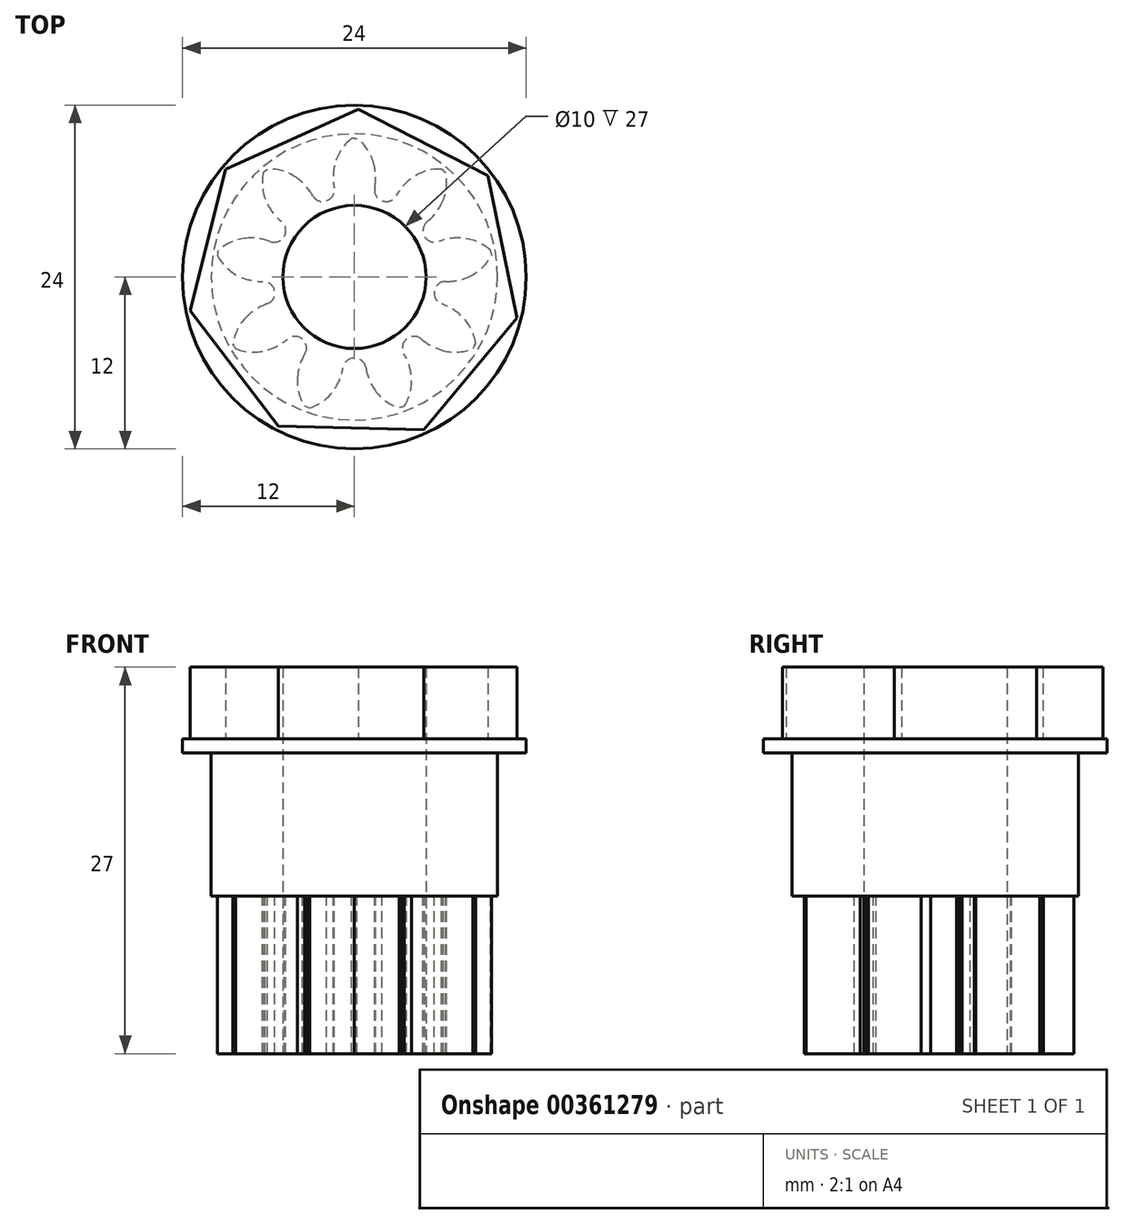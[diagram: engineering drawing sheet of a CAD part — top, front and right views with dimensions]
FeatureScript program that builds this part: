
annotation { "Feature Type Name" : "Feature", "Feature Type Description" : "" }
export const myFeature = defineFeature(function(context is Context, id is Id, definition is map)
    precondition{}
    {
        {
            var Q0;
            Q0=qCreatedBy(makeId("Top.planeOp"),FACE);
            var sketch = newSketch(context, id + "F0", { "sketchPlane" : qUnion([Q0])});
            skCircle(sketch, "E0", {"center": v(0, 0) * mm, "radius": 7.9 * mm, "construction": true});
            skCircle(sketch, "E1", {"center": v(0, 0) * mm, "radius": 9.68 * mm, "construction": true});
            skCircle(sketch, "E2", {"center": v(0, 0) * mm, "radius": 5.68 * mm, "construction": true});
            skCircle(sketch, "E3", {"center": v(0, 7.9) * mm, "radius": 1.4 * mm, "construction": true});
            skCircle(sketch, "E4", {"center": v(0, 0) * mm, "radius": 7.3 * mm, "construction": true});
            skCircle(sketch, "E5", {"center": v(1.39, 7.78) * mm, "radius": 3.3 * mm, "construction": true});
            skCircle(sketch, "E6", {"center": v(0, 0) * mm, "radius": 5 * mm});
            skCircle(sketch, "E7", {"center": v(1.39, 7.78) * mm, "radius": 3.77 * mm, "construction": true});
            skArc(sketch, "E8", {"start": v(1.42, 6.23) * mm, "mid": v(1.48, 7) * mm, "end": v(1.39, 7.78) * mm});
            skArc(sketch, "E9.trimOffspring", {"start": v(1.39, 7.78) * mm, "mid": v(0.96, 8.83) * mm, "end": v(0.19, 9.68) * mm});
            skLineSegment(sketch, "E10", {"start": v(2.17, 5.25) * mm, "end": v(1.96, 5.31) * mm});
            skLineSegment(sketch, "E11", {"start": v(0, 9.68) * mm, "end": v(0.19, 9.68) * mm});
            skPoint(sketch, "E12.visualSharp", {"position": v(1.22, 5.55) * mm});
            skArc(sketch, "E12.filletArc", {"start": v(1.42, 6.23) * mm, "mid": v(1.52, 5.67) * mm, "end": v(1.96, 5.31) * mm});
            skLineSegment(sketch, "E13.MirrorCS", {"start": v(-2.17, 5.25) * mm, "end": v(-1.96, 5.31) * mm});
            skLineSegment(sketch, "E14.MirrorCS", {"start": v(0, 9.68) * mm, "end": v(-0.19, 9.68) * mm});
            skArc(sketch, "E15.MirrorCS", {"start": v(-1.39, 7.78) * mm, "mid": v(-0.96, 8.83) * mm, "end": v(-0.19, 9.68) * mm});
            skArc(sketch, "E16.MirrorCS", {"start": v(-1.42, 6.23) * mm, "mid": v(-1.48, 7) * mm, "end": v(-1.39, 7.78) * mm});
            skArc(sketch, "E17.MirrorCS", {"start": v(-1.42, 6.23) * mm, "mid": v(-1.52, 5.67) * mm, "end": v(-1.96, 5.31) * mm});
            skLineSegment(sketch, "E18.1.0", {"start": v(-5.04, 2.62) * mm, "end": v(-4.92, 2.8) * mm});
            skArc(sketch, "E18.1.1", {"start": v(-5.09, 3.86) * mm, "mid": v(-4.8, 3.37) * mm, "end": v(-4.92, 2.8) * mm});
            skArc(sketch, "E18.1.2", {"start": v(-5.09, 3.86) * mm, "mid": v(-5.64, 4.41) * mm, "end": v(-6.06, 5.06) * mm});
            skArc(sketch, "E18.1.3", {"start": v(-6.06, 5.06) * mm, "mid": v(-6.4, 6.15) * mm, "end": v(-6.37, 7.3) * mm});
            skLineSegment(sketch, "E18.1.4", {"start": v(-6.22, 7.42) * mm, "end": v(-6.37, 7.3) * mm});
            skLineSegment(sketch, "E18.1.5", {"start": v(-6.22, 7.42) * mm, "end": v(-6.08, 7.54) * mm});
            skArc(sketch, "E18.1.6", {"start": v(-3.93, 6.85) * mm, "mid": v(-4.95, 7.38) * mm, "end": v(-6.08, 7.54) * mm});
            skArc(sketch, "E18.1.7", {"start": v(-2.92, 5.68) * mm, "mid": v(-3.37, 6.32) * mm, "end": v(-3.93, 6.85) * mm});
            skArc(sketch, "E18.1.8", {"start": v(-2.92, 5.68) * mm, "mid": v(-2.48, 5.32) * mm, "end": v(-1.91, 5.33) * mm});
            skLineSegment(sketch, "E18.1.9", {"start": v(-1.7, 5.42) * mm, "end": v(-1.91, 5.33) * mm});
            skLineSegment(sketch, "E18.2.0", {"start": v(-5.55, -1.23) * mm, "end": v(-5.57, -1.01) * mm});
            skArc(sketch, "E18.2.1", {"start": v(-6.38, -0.31) * mm, "mid": v(-5.84, -0.5) * mm, "end": v(-5.57, -1.01) * mm});
            skArc(sketch, "E18.2.2", {"start": v(-6.38, -0.31) * mm, "mid": v(-7.15, -0.25) * mm, "end": v(-7.9, -0.02) * mm});
            skArc(sketch, "E18.2.3", {"start": v(-7.9, -0.02) * mm, "mid": v(-8.86, 0.6) * mm, "end": v(-9.56, 1.5) * mm});
            skLineSegment(sketch, "E18.2.4", {"start": v(-9.53, 1.68) * mm, "end": v(-9.56, 1.5) * mm});
            skLineSegment(sketch, "E18.2.5", {"start": v(-9.53, 1.68) * mm, "end": v(-9.5, 1.87) * mm});
            skArc(sketch, "E18.2.6", {"start": v(-7.42, 2.72) * mm, "mid": v(-8.53, 2.48) * mm, "end": v(-9.5, 1.87) * mm});
            skArc(sketch, "E18.2.7", {"start": v(-5.89, 2.48) * mm, "mid": v(-6.64, 2.68) * mm, "end": v(-7.42, 2.72) * mm});
            skArc(sketch, "E18.2.8", {"start": v(-5.89, 2.48) * mm, "mid": v(-5.32, 2.48) * mm, "end": v(-4.9, 2.86) * mm});
            skLineSegment(sketch, "E18.2.9", {"start": v(-4.8, 3.05) * mm, "end": v(-4.9, 2.86) * mm});
            skLineSegment(sketch, "E18.3.0", {"start": v(-3.46, -4.5) * mm, "end": v(-3.62, -4.36) * mm});
            skArc(sketch, "E18.3.1", {"start": v(-4.68, -4.34) * mm, "mid": v(-4.15, -4.15) * mm, "end": v(-3.62, -4.36) * mm});
            skArc(sketch, "E18.3.2", {"start": v(-4.68, -4.34) * mm, "mid": v(-5.32, -4.79) * mm, "end": v(-6.04, -5.1) * mm});
            skArc(sketch, "E18.3.3", {"start": v(-6.04, -5.1) * mm, "mid": v(-7.17, -5.24) * mm, "end": v(-8.29, -5) * mm});
            skLineSegment(sketch, "E18.3.4", {"start": v(-8.38, -4.84) * mm, "end": v(-8.29, -5) * mm});
            skLineSegment(sketch, "E18.3.5", {"start": v(-8.38, -4.84) * mm, "end": v(-8.48, -4.68) * mm});
            skArc(sketch, "E18.3.6", {"start": v(-7.43, -2.69) * mm, "mid": v(-8.13, -3.59) * mm, "end": v(-8.48, -4.68) * mm});
            skArc(sketch, "E18.3.7", {"start": v(-6.1, -1.89) * mm, "mid": v(-6.8, -2.22) * mm, "end": v(-7.43, -2.69) * mm});
            skArc(sketch, "E18.3.8", {"start": v(-6.1, -1.89) * mm, "mid": v(-5.67, -1.52) * mm, "end": v(-5.58, -0.96) * mm});
            skLineSegment(sketch, "E18.3.9", {"start": v(-5.63, -0.74) * mm, "end": v(-5.58, -0.96) * mm});
            skLineSegment(sketch, "E18.4.0", {"start": v(0.25, -5.67) * mm, "end": v(0.03, -5.66) * mm});
            skArc(sketch, "E18.4.1", {"start": v(-0.8, -6.34) * mm, "mid": v(-0.51, -5.84) * mm, "end": v(0.03, -5.66) * mm});
            skArc(sketch, "E18.4.2", {"start": v(-0.8, -6.34) * mm, "mid": v(-1, -7.09) * mm, "end": v(-1.35, -7.78) * mm});
            skArc(sketch, "E18.4.3", {"start": v(-1.35, -7.78) * mm, "mid": v(-2.12, -8.63) * mm, "end": v(-3.13, -9.16) * mm});
            skLineSegment(sketch, "E18.4.4", {"start": v(-3.31, -9.1) * mm, "end": v(-3.13, -9.16) * mm});
            skLineSegment(sketch, "E18.4.5", {"start": v(-3.31, -9.1) * mm, "end": v(-3.49, -9.03) * mm});
            skArc(sketch, "E18.4.6", {"start": v(-3.97, -6.83) * mm, "mid": v(-3.92, -7.97) * mm, "end": v(-3.49, -9.03) * mm});
            skArc(sketch, "E18.4.7", {"start": v(-3.46, -5.37) * mm, "mid": v(-3.79, -6.07) * mm, "end": v(-3.97, -6.83) * mm});
            skArc(sketch, "E18.4.8", {"start": v(-3.46, -5.37) * mm, "mid": v(-3.36, -4.8) * mm, "end": v(-3.66, -4.32) * mm});
            skLineSegment(sketch, "E18.4.9", {"start": v(-3.84, -4.19) * mm, "end": v(-3.66, -4.32) * mm});
            skLineSegment(sketch, "E18.5.0", {"start": v(3.84, -4.19) * mm, "end": v(3.66, -4.32) * mm});
            skArc(sketch, "E18.5.1", {"start": v(3.46, -5.37) * mm, "mid": v(3.36, -4.8) * mm, "end": v(3.66, -4.32) * mm});
            skArc(sketch, "E18.5.2", {"start": v(3.46, -5.37) * mm, "mid": v(3.79, -6.07) * mm, "end": v(3.97, -6.83) * mm});
            skArc(sketch, "E18.5.3", {"start": v(3.97, -6.83) * mm, "mid": v(3.92, -7.97) * mm, "end": v(3.49, -9.03) * mm});
            skLineSegment(sketch, "E18.5.4", {"start": v(3.31, -9.1) * mm, "end": v(3.49, -9.03) * mm});
            skLineSegment(sketch, "E18.5.5", {"start": v(3.31, -9.1) * mm, "end": v(3.13, -9.16) * mm});
            skArc(sketch, "E18.5.6", {"start": v(1.35, -7.78) * mm, "mid": v(2.12, -8.63) * mm, "end": v(3.13, -9.16) * mm});
            skArc(sketch, "E18.5.7", {"start": v(0.8, -6.34) * mm, "mid": v(1, -7.09) * mm, "end": v(1.35, -7.78) * mm});
            skArc(sketch, "E18.5.8", {"start": v(0.8, -6.34) * mm, "mid": v(0.51, -5.84) * mm, "end": v(-0.03, -5.66) * mm});
            skLineSegment(sketch, "E18.5.9", {"start": v(-0.25, -5.67) * mm, "end": v(-0.03, -5.66) * mm});
            skLineSegment(sketch, "E18.6.0", {"start": v(5.63, -0.74) * mm, "end": v(5.58, -0.96) * mm});
            skArc(sketch, "E18.6.1", {"start": v(6.1, -1.89) * mm, "mid": v(5.67, -1.52) * mm, "end": v(5.58, -0.96) * mm});
            skArc(sketch, "E18.6.2", {"start": v(6.1, -1.89) * mm, "mid": v(6.8, -2.22) * mm, "end": v(7.43, -2.69) * mm});
            skArc(sketch, "E18.6.3", {"start": v(7.43, -2.69) * mm, "mid": v(8.13, -3.59) * mm, "end": v(8.48, -4.68) * mm});
            skLineSegment(sketch, "E18.6.4", {"start": v(8.38, -4.84) * mm, "end": v(8.48, -4.68) * mm});
            skLineSegment(sketch, "E18.6.5", {"start": v(8.38, -4.84) * mm, "end": v(8.29, -5) * mm});
            skArc(sketch, "E18.6.6", {"start": v(6.04, -5.1) * mm, "mid": v(7.17, -5.24) * mm, "end": v(8.29, -5) * mm});
            skArc(sketch, "E18.6.7", {"start": v(4.68, -4.34) * mm, "mid": v(5.32, -4.79) * mm, "end": v(6.04, -5.1) * mm});
            skArc(sketch, "E18.6.8", {"start": v(4.68, -4.34) * mm, "mid": v(4.15, -4.15) * mm, "end": v(3.62, -4.36) * mm});
            skLineSegment(sketch, "E18.6.9", {"start": v(3.46, -4.5) * mm, "end": v(3.62, -4.36) * mm});
            skLineSegment(sketch, "E18.7.0", {"start": v(4.8, 3.05) * mm, "end": v(4.9, 2.86) * mm});
            skArc(sketch, "E18.7.1", {"start": v(5.89, 2.48) * mm, "mid": v(5.32, 2.48) * mm, "end": v(4.9, 2.86) * mm});
            skArc(sketch, "E18.7.2", {"start": v(5.89, 2.48) * mm, "mid": v(6.64, 2.68) * mm, "end": v(7.42, 2.72) * mm});
            skArc(sketch, "E18.7.3", {"start": v(7.42, 2.72) * mm, "mid": v(8.53, 2.48) * mm, "end": v(9.5, 1.87) * mm});
            skLineSegment(sketch, "E18.7.4", {"start": v(9.53, 1.68) * mm, "end": v(9.5, 1.87) * mm});
            skLineSegment(sketch, "E18.7.5", {"start": v(9.53, 1.68) * mm, "end": v(9.56, 1.5) * mm});
            skArc(sketch, "E18.7.6", {"start": v(7.9, -0.02) * mm, "mid": v(8.86, 0.6) * mm, "end": v(9.56, 1.5) * mm});
            skArc(sketch, "E18.7.7", {"start": v(6.38, -0.31) * mm, "mid": v(7.15, -0.25) * mm, "end": v(7.9, -0.02) * mm});
            skArc(sketch, "E18.7.8", {"start": v(6.38, -0.31) * mm, "mid": v(5.84, -0.5) * mm, "end": v(5.57, -1.01) * mm});
            skLineSegment(sketch, "E18.7.9", {"start": v(5.55, -1.23) * mm, "end": v(5.57, -1.01) * mm});
            skLineSegment(sketch, "E18.8.0", {"start": v(1.7, 5.42) * mm, "end": v(1.91, 5.33) * mm});
            skArc(sketch, "E18.8.1", {"start": v(2.92, 5.68) * mm, "mid": v(2.48, 5.32) * mm, "end": v(1.91, 5.33) * mm});
            skArc(sketch, "E18.8.2", {"start": v(2.92, 5.68) * mm, "mid": v(3.37, 6.32) * mm, "end": v(3.93, 6.85) * mm});
            skArc(sketch, "E18.8.3", {"start": v(3.93, 6.85) * mm, "mid": v(4.95, 7.38) * mm, "end": v(6.08, 7.54) * mm});
            skLineSegment(sketch, "E18.8.4", {"start": v(6.22, 7.42) * mm, "end": v(6.08, 7.54) * mm});
            skLineSegment(sketch, "E18.8.5", {"start": v(6.22, 7.42) * mm, "end": v(6.37, 7.3) * mm});
            skArc(sketch, "E18.8.6", {"start": v(6.06, 5.06) * mm, "mid": v(6.4, 6.15) * mm, "end": v(6.37, 7.3) * mm});
            skArc(sketch, "E18.8.7", {"start": v(5.09, 3.86) * mm, "mid": v(5.64, 4.41) * mm, "end": v(6.06, 5.06) * mm});
            skArc(sketch, "E18.8.8", {"start": v(5.09, 3.86) * mm, "mid": v(4.8, 3.37) * mm, "end": v(4.92, 2.8) * mm});
            skLineSegment(sketch, "E18.8.9", {"start": v(5.04, 2.62) * mm, "end": v(4.92, 2.8) * mm});
            skCircle(sketch, "E19", {"center": v(0, 0) * mm, "radius": 10 * mm});
            skCircle(sketch, "E20.cCircle", {"center": v(0, 0) * mm, "radius": 10.55 * mm, "construction": true});
            skLineSegment(sketch, "E20.0", {"start": v(11.35, -2.87) * mm, "end": v(4.84, -10.66) * mm});
            skLineSegment(sketch, "E20.1", {"start": v(4.84, -10.66) * mm, "end": v(-5.32, -10.43) * mm});
            skLineSegment(sketch, "E20.2", {"start": v(-5.32, -10.43) * mm, "end": v(-11.47, -2.34) * mm});
            skLineSegment(sketch, "E20.3", {"start": v(-11.47, -2.34) * mm, "end": v(-8.98, 7.5) * mm});
            skLineSegment(sketch, "E20.4", {"start": v(-8.98, 7.5) * mm, "end": v(0.27, 11.7) * mm});
            skLineSegment(sketch, "E20.5", {"start": v(0.27, 11.7) * mm, "end": v(9.32, 7.09) * mm});
            skLineSegment(sketch, "E20.6", {"start": v(9.32, 7.09) * mm, "end": v(11.35, -2.87) * mm});
            skPoint(sketch, "E20.0.midPoint", {"position": v(8.1, -6.77) * mm});
            skCircle(sketch, "E21", {"center": v(0, 0) * mm, "radius": 12 * mm});
            skSolve(sketch);
        }
        {
            var Q0;
            Q0=makeQuery(id+"F0.imprint","IMPRINT",FACE,{"disambiguationData":[TD([[makeQuery(id+"F0.imprint","IMPRINT",EDGE,{"derivedFrom":sQuery(id+"F0.wireOp",EDGE,"E6")}),-1.0]])]});
            extrude(context, id + "F1", {"entities" : qUnion([Q0]), "depth" : 16 * mm});
        }
        {
            var Q0;
            {var subQ80=sQuery(id+"F0.wireOp",EDGE,"E8");Q0=makeQuery(id+"F0.imprint","IMPRINT",FACE,{"disambiguationData":[TD([[makeQuery(id+"F0.imprint","IMPRINT",EDGE,{"derivedFrom":subQ80}),-1.0]])]});}
            extrude(context, id + "F2", {"entities" : qUnion([Q0]), "operationType" : NewBodyOperationType.ADD, "depth" : 16 * mm});
        }
        {
            var Q0;
            Q0=makeQuery(id+"F0.imprint","IMPRINT",FACE,{"disambiguationData":[TD([[makeQuery(id+"F0.imprint","IMPRINT",EDGE,{"derivedFrom":sQuery(id+"F0.wireOp",EDGE,"E19")}),-1.0]])]});
            extrude(context, id + "F3", {"entities" : qUnion([Q0]), "operationType" : NewBodyOperationType.ADD, "depth" : 16 * mm});
        }
        {
            var Q0;
            Q0=makeQuery(id+"F0.imprint","IMPRINT",FACE,{"disambiguationData":[TD([[makeQuery(id+"F0.imprint","IMPRINT",EDGE,{"derivedFrom":sQuery(id+"F0.wireOp",EDGE,"E20.0")}),1.0]])]});
            extrude(context, id + "F4", {"entities" : qUnion([Q0]), "operationType" : NewBodyOperationType.ADD, "depth" : 11 * mm});
        }
        {
            var Q0;
            Q0=makeQuery(id+"F0.imprint","IMPRINT",FACE,{"disambiguationData":[TD([[makeQuery(id+"F0.imprint","IMPRINT",EDGE,{"derivedFrom":sQuery(id+"F0.wireOp",EDGE,"E20.0")}),1.0]])]});
            extrude(context, id + "F5", {"entities" : qUnion([Q0]), "operationType" : NewBodyOperationType.REMOVE, "depth" : 10 * mm});
        }
        {
            var Q0;
            Q0=makeQuery(id+"F0.imprint","IMPRINT",FACE,{"disambiguationData":[TD([[makeQuery(id+"F0.imprint","IMPRINT",EDGE,{"derivedFrom":sQuery(id+"F0.wireOp",EDGE,"E19")}),-1.0]])]});
            extrude(context, id + "F6", {"entities" : qUnion([Q0]), "operationType" : NewBodyOperationType.REMOVE, "depth" : 10 * mm});
        }
        {
            var Q0;
            Q0=makeQuery(id+"F0.imprint","IMPRINT",FACE,{"disambiguationData":[TD([[makeQuery(id+"F0.imprint","IMPRINT",EDGE,{"derivedFrom":sQuery(id+"F0.wireOp",EDGE,"E6")}),-1.0]])]});
            extrude(context, id + "F7", {"entities" : qUnion([Q0]), "operationType" : NewBodyOperationType.ADD, "oppositeDirection" : true, "depth" : 11 * mm});
        }
    });
